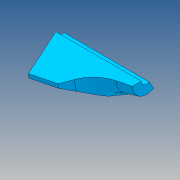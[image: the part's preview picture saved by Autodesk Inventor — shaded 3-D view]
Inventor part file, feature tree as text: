
AUTODESK INVENTOR PART (.ipt)
format: ipt  version: 2017 (Build 210142000, 142)  size: 143,360 bytes
history: native  units: mm
features: revolve x2, plane x2, chamfer x2, sketch x1, split x1, mirror x1
ambient origin geometry x8: Origin, YZ Plane, XZ Plane, XY Plane, X Axis, Y Axis, Z Axis, Center Point
bodies: Solid1 (feature_tree)
feature tree (9):
  sketch  "Sketch1"  dims[d0=45.0deg d1=3.0mm d2=2.443461mm d6=10.0mm d7=14.0mm d8=15.0mm d9=3.0mm d10=75.0mm d11=8.0mm d12=2.443461mm d13=120.0deg d14=2.0mm d15=2.0mm d16=90.0deg d17=2.0mm d18=2.0mm d19=90.0deg d20=60.0deg d21=0.087266mm]
  revolve  "Revolution1"  [1 undecoded]
  plane  "Work Plane1"
  split  "Split1"
  chamfer  "Chamfer1"  Distance=2.443461mm
  chamfer  "Chamfer2"  Distance=10.0mm
  plane  "Work Plane2"
  revolve  "Revolution2"  [1 undecoded]
  mirror  "Mirror1"
note: 2 required parameter values undecoded (feature->parameter linkage not recoverable at this tier; creation-order binding heuristic only, values carry confidence <= 0.55)
